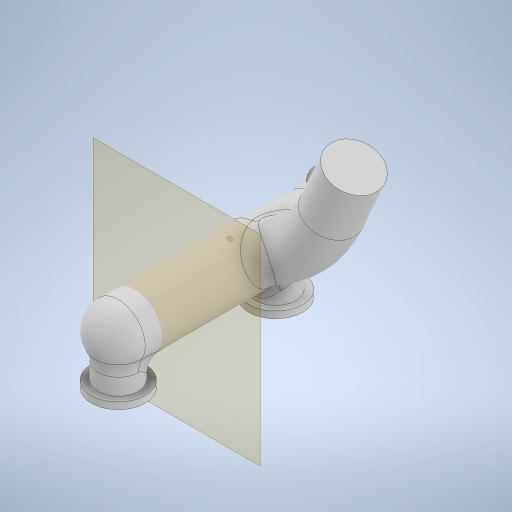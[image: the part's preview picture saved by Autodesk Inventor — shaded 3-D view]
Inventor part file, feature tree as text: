
AUTODESK INVENTOR PART (.ipt)
format: ipt  version: 2023 (Build 270158000, 158)  size: 774,656 bytes
history: native  units: in
note: dims shown in document units (in); Inventor stores cm internally (conversion verified against a paired STEP export)
features: sketch x7, extrude x5, plane x3, fillet x3, other x2, revolve x1, loft x1, sweep x1, mirror x1, projected_geometry x1
ambient origin geometry x8: Origin, YZ Plane, XZ Plane, XY Plane, X Axis, Y Axis, Z Axis, Center Point
bodies: Solid1 (feature_tree)
feature tree (25):
  other  "intake_manifold_f"
  revolve  "Revolution1"  [1 undecoded]
  plane  "Work Plane1"
  loft  "Loft1"
  extrude  "Extrusion1"  Depth=2.0in
  fillet  "Fillet1"  Radius=0.3937in
  extrude  "Extrusion2"  Depth=9.0in
  extrude  "Extrusion3"  Depth=11.0in TaperAngle=0.0deg
  extrude  "Extrusion4"  Depth=12.0in
  plane  "Work Plane3"
  sketch  "Sketch9"  dims[d20=12.0in d21=12.0in]
  plane  "Work Plane2"
  sweep  "Sweep2"
  fillet  "Fillet5"  Radius=1.0in
  extrude  "Extrusion6"  Depth=8.0in
  mirror  "Mirror3"
  fillet  "Fillet7"  Radius=5.25in
  sketch  "Sketch3"  dims[d3=30.0in d4=6.0in]
  other  "Edges1"
  sketch  "Sketch4"  dims[d5=90.0deg d6=12.0in]
  sketch  "Sketch5"  dims[d7=8.0in d8=2.0in d9=0.3937in d10=90.0deg]
  projected_geometry  "Projected Loop1"
  sketch  "Sketch6"  dims[d13=0.3937in d14=90.0deg d15=9.0in]
  sketch  "Sketch7"  dims[d16=9.0in d17=11.0in d18=0.0in]
  sketch  "Sketch10"  dims[d22=1.5in d23=0.0in d24=6.0in d25=6.0in d26=6.0in d27=0.0in d28=2.0in d29=0.1969in d30=6.0in d31=0.3937in d33=1.0in d34=0.0in d35=8.0in d36=5.25in d37=0.0in d52=11.0in d56=0.0in d57=0.0in d58=3.0in d59=0.0in d60=5.0in d61=11.0in d62=1.5in d63=0.0in d74=2.5in d75=13.78in d76=3.0in]
note: 1 required parameter value undecoded (feature->parameter linkage not recoverable at this tier; creation-order binding heuristic only, values carry confidence <= 0.55)
